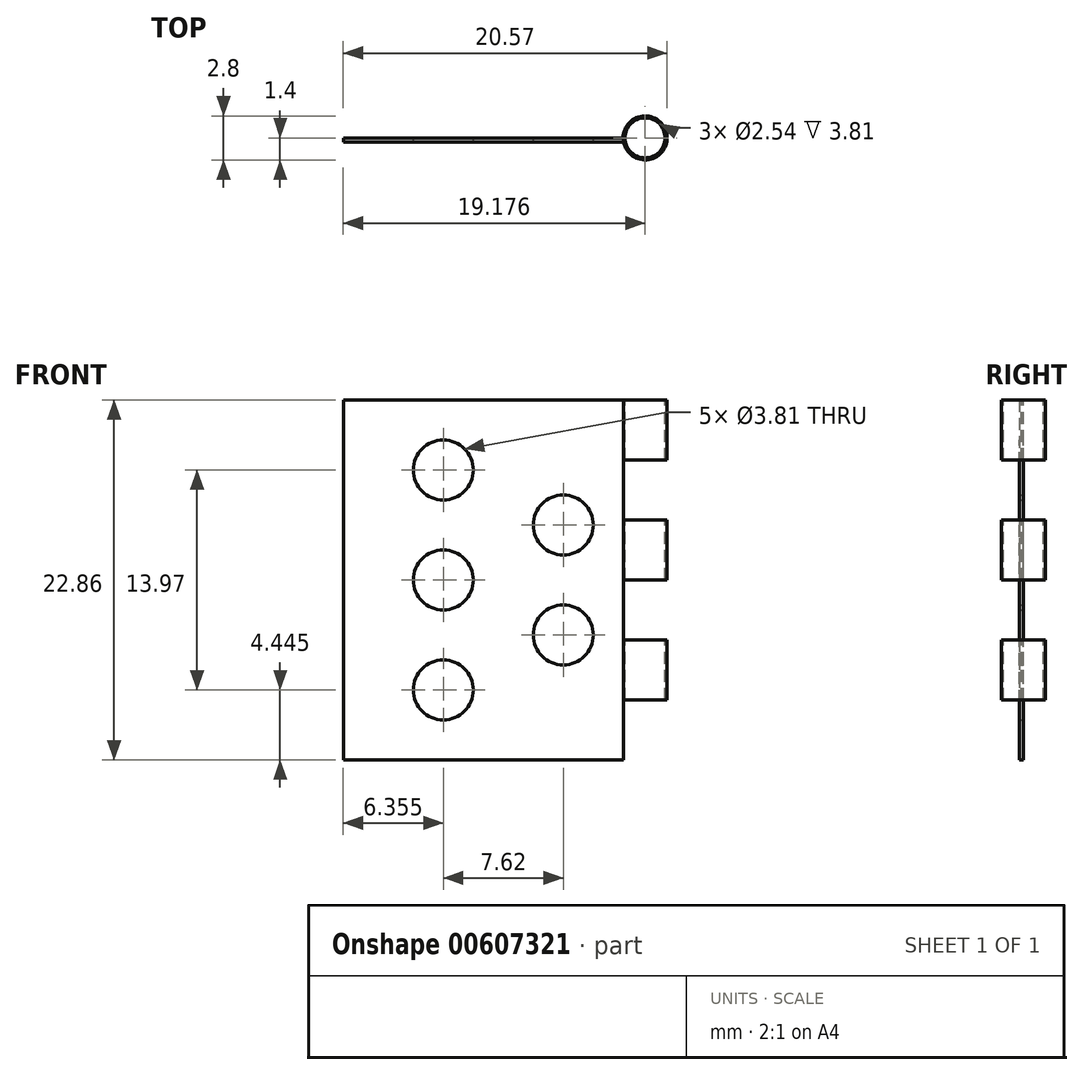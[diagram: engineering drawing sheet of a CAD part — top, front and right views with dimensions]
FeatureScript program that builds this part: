
annotation { "Feature Type Name" : "Feature", "Feature Type Description" : "" }
export const myFeature = defineFeature(function(context is Context, id is Id, definition is map)
    precondition{}
    {
        {
            var Q0;
            Q0=qCreatedBy(makeId("Front.planeOp"),FACE);
            var sketch = newSketch(context, id + "F0", { "sketchPlane" : qUnion([Q0])});
            skLineSegment(sketch, "E0", {"start": v(8.84, 0) * mm, "end": v(8.84, -22.86) * mm});
            skLineSegment(sketch, "E1", {"start": v(8.84, -22.86) * mm, "end": v(-8.94, -22.86) * mm});
            skLineSegment(sketch, "E2", {"start": v(-8.94, -22.86) * mm, "end": v(-8.94, 0) * mm});
            skLineSegment(sketch, "E3", {"start": v(-8.94, 0) * mm, "end": v(8.84, 0) * mm});
            skCircle(sketch, "E4", {"center": v(5.03, -14.92) * mm, "radius": 1.9 * mm});
            skCircle(sketch, "E5", {"center": v(-2.59, -11.43) * mm, "radius": 1.9 * mm});
            skCircle(sketch, "E6", {"center": v(5.03, -7.94) * mm, "radius": 1.9 * mm});
            skCircle(sketch, "E7", {"center": v(-2.59, -4.44) * mm, "radius": 1.9 * mm});
            skCircle(sketch, "E8", {"center": v(-2.59, -18.41) * mm, "radius": 1.9 * mm});
            skLineSegment(sketch, "E9", {"start": v(-2.59, -22.86) * mm, "end": v(-2.59, 0) * mm, "construction": true});
            skLineSegment(sketch, "E10", {"start": v(5.03, -22.86) * mm, "end": v(5.03, 0) * mm, "construction": true});
            skSolve(sketch);
        }
        {
            var Q0;
            Q0=makeQuery(id+"F0.imprint","IMPRINT",FACE,{"disambiguationData":[TD([[makeQuery(id+"F0.imprint","IMPRINT",EDGE,{"derivedFrom":sQuery(id+"F0.wireOp",EDGE,"E0")}),-1.0]])]});
            extrude(context, id + "F1", {"entities" : qUnion([Q0]), "depth" : 0.25 * mm, "offsetDistance" : 25.4 * mm});
        }
        {
            var Q0;
            Q0=qCreatedBy(makeId("Top.planeOp"),FACE);
            var sketch = newSketch(context, id + "F2", { "sketchPlane" : qUnion([Q0])});
            skCircle(sketch, "E11", {"center": v(10.24, 0) * mm, "radius": 1.4 * mm});
            skSolve(sketch);
        }
        {
            var Q0;
            Q0=makeQuery(id+"F2.imprint","IMPRINT",FACE,{"disambiguationData":[TD([[makeQuery(id+"F2.imprint","IMPRINT",EDGE,{"derivedFrom":sQuery(id+"F2.wireOp",EDGE,"E11")}),1.0]])]});
            extrude(context, id + "F3", {"entities" : qUnion([Q0]), "operationType" : NewBodyOperationType.ADD, "oppositeDirection" : true, "depth" : 3.8 * mm, "offsetDistance" : 25.4 * mm});
        }
        {
            var Q0;
            Q0=qCreatedBy(makeId("Top.planeOp"),FACE);
            cPlane(context, id + "F4", {"entities" : qUnion([Q0]), "cplaneType" : CPlaneType.OFFSET, "offset" : 7.62 * mm, "oppositeDirection" : true, "width" : 152.4 * mm, "height" : 152.4 * mm});
        }
        {
            var Q0;
            Q0=qCreatedBy(id+"F4.planeOp",FACE);
            var sketch = newSketch(context, id + "F5", { "sketchPlane" : qUnion([Q0])});
            skCircle(sketch, "E12", {"center": v(10.24, 0) * mm, "radius": 1.4 * mm});
            skSolve(sketch);
        }
        {
            var Q0;
            Q0 = qSketchRegion(id + "F5", true);
            extrude(context, id + "F6", {"entities" : qUnion([Q0]), "operationType" : NewBodyOperationType.ADD, "oppositeDirection" : true, "depth" : 3.8 * mm, "offsetDistance" : 25.4 * mm});
        }
        {
            var Q0;
            Q0=qCreatedBy(id+"F4.planeOp",FACE);
            cPlane(context, id + "F7", {"entities" : qUnion([Q0]), "cplaneType" : CPlaneType.OFFSET, "offset" : 7.62 * mm, "oppositeDirection" : true, "width" : 152.4 * mm, "height" : 152.4 * mm});
        }
        {
            var Q0;
            Q0=qCreatedBy(id+"F7.planeOp",FACE);
            var sketch = newSketch(context, id + "F8", { "sketchPlane" : qUnion([Q0])});
            skCircle(sketch, "E13", {"center": v(10.24, 0) * mm, "radius": 1.4 * mm});
            skSolve(sketch);
        }
        {
            var Q0;
            Q0=makeQuery(id+"F8.imprint","IMPRINT",FACE,{"disambiguationData":[TD([[makeQuery(id+"F8.imprint","IMPRINT",EDGE,{"derivedFrom":sQuery(id+"F8.wireOp",EDGE,"E13")}),1.0]])]});
            extrude(context, id + "F9", {"entities" : qUnion([Q0]), "operationType" : NewBodyOperationType.ADD, "oppositeDirection" : true, "depth" : 3.8 * mm, "offsetDistance" : 25.4 * mm});
        }
        {
            var Q0;
            Q0=sQuery(id+"F2.wireOp",VERTEX,"E11.center");
            var Q1;
            Q1=makeQuery(id+"F1.opExtrude","SWEPT_BODY",BODY,{"disambiguationData":[OSD([sQuery(id+"F0.wireOp",EDGE,"E0"),sQuery(id+"F0.wireOp",EDGE,"E1"),sQuery(id+"F0.wireOp",EDGE,"E2"),sQuery(id+"F0.wireOp",EDGE,"E3")])]});
            hole(context, id + "F10", {"style" : HoleStyle.SIMPLE, "endStyle" : HoleEndStyle.THROUGH, "holeDiameter" : 2.54 * mm, "majorDiameter" : 6.35 * mm, "isTappedThrough" : true, "tappedDepth" : 12.7 * mm, "tapClearance" : 3, "locations" : qUnion([Q0]), "scope" : qUnion([Q1])});
        }
    });
